# Revit family: Hitachi_Remote-Controller-PC-ARFPE_
name_source: partatom
category: Mechanical Equipment
revit_build: Autodesk Revit 2018 (Build: 20190510_1515(x64)
units: mm (PartAtom-declared; Revit-internal decimal feet)

## family parameters
Always vertical = Yes
Classification = None
Cut with Voids When Loaded = No
OmniClass Number = 23.75.65.14.17
OmniClass Title = Control and Monitoring Boards/Panels
Part Type = Normal
Room Calculation Point = No
Round Connector Dimension = Use Diameter
Shared = No
Work Plane-Based = Yes

## types (1)
- PC-ARFP1E
    BC_MODEL_ID = 350137
    BC_OBJECT_ID = 37817
    BC_OBJECT_VERSION = #5
    BC_VARIANT_ID = 230767
    Color = White
    Communication Type = Wired
    Default Elevation = 1219 mm
    Description = Remote Controller PC-ARFPE
    ETIM Code = EC011603
    Electric Power = 0 W
    Frequency = 0 Hz
    Manufacturer = Hitachi Air Conditioning Europe SAS
    Mass = 0.17 kg
    MasterFormat = Electric and Electronic Control System for HVAC
    Masterformat Code = 23 09 33
    Maximum Operating Temperature = 35 °C
    Minimum Operating Temperature = 5 °C
    Model = Remote Controller PC-ARFPE
    Name = Remote Controller PC-ARFPE
    Name BIM&CO = Panneau de contrôle
    Name ETIM = Accessoires pour climatiseur
    Nominal Current = 0 A
    Nominal Voltage = 0 V
    OMNICLASS Table 23 Code  = 23-27 15 23 11
    Object type = Control Panel
    Omniclass = HVAC Main Control Panels
    Operating Humidity Range = 35~90%
    Overall Depth = 18 mm
    Overall Height = 110 mm  [stored 0.360892 ft]
    Overall Width = 120 mm  [stored 0.393701 ft]
    Reference description = Remote Controller PC-ARFPE
    Type Comments = Remote Controller PC-ARFPE
    Uniformat = Contrôle électronique
    Uniformat code = D306002

note: [stored X ft] marks values corroborated as IEEE doubles in the binary element streams (Revit-internal decimal feet)

## geometry (parser evidence)
native form markers: Sweep x2
no freeform markers — native parametric forms only
